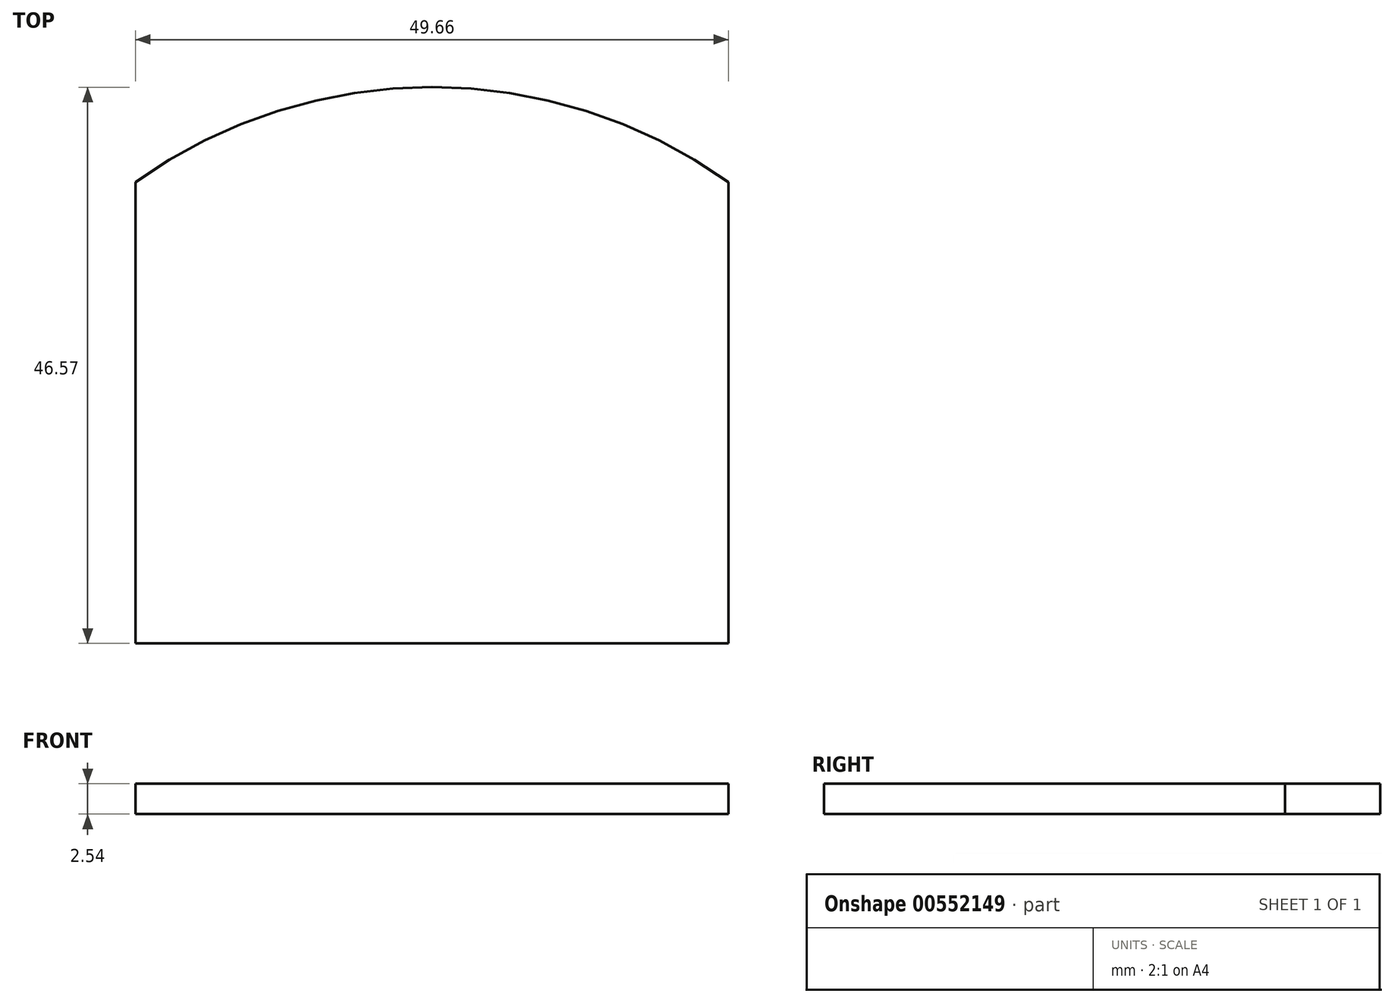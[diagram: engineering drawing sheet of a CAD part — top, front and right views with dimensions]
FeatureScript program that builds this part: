
annotation { "Feature Type Name" : "Feature", "Feature Type Description" : "" }
export const myFeature = defineFeature(function(context is Context, id is Id, definition is map)
    precondition{}
    {
        {
            var Q0;
            Q0=qCreatedBy(makeId("Top.planeOp"),FACE);
            var sketch = newSketch(context, id + "F0", { "sketchPlane" : qUnion([Q0])});
            skLineSegment(sketch, "E0.bottom", {"start": v(24.83, -19.31) * mm, "end": v(-24.83, -19.31) * mm});
            skLineSegment(sketch, "E0.top", {"start": v(24.83, 19.31) * mm, "end": v(-24.83, 19.31) * mm});
            skLineSegment(sketch, "E0.left", {"start": v(24.83, -19.31) * mm, "end": v(24.83, 19.31) * mm});
            skLineSegment(sketch, "E0.right", {"start": v(-24.83, -19.31) * mm, "end": v(-24.83, 19.31) * mm});
            skPoint(sketch, "E0.middle", {"position": v(0, 0) * mm});
            skArc(sketch, "E1", {"start": v(24.83, 19.31) * mm, "mid": v(0, 27.26) * mm, "end": v(-24.83, 19.31) * mm});
            skSolve(sketch);
        }
        {
            var Q0;
            Q0 = qSketchRegion(id + "F0", true);
            extrude(context, id + "F1", {"entities" : qUnion([Q0]), "depth" : 2.54 * mm, "offsetDistance" : 25.4 * mm});
        }
    });
